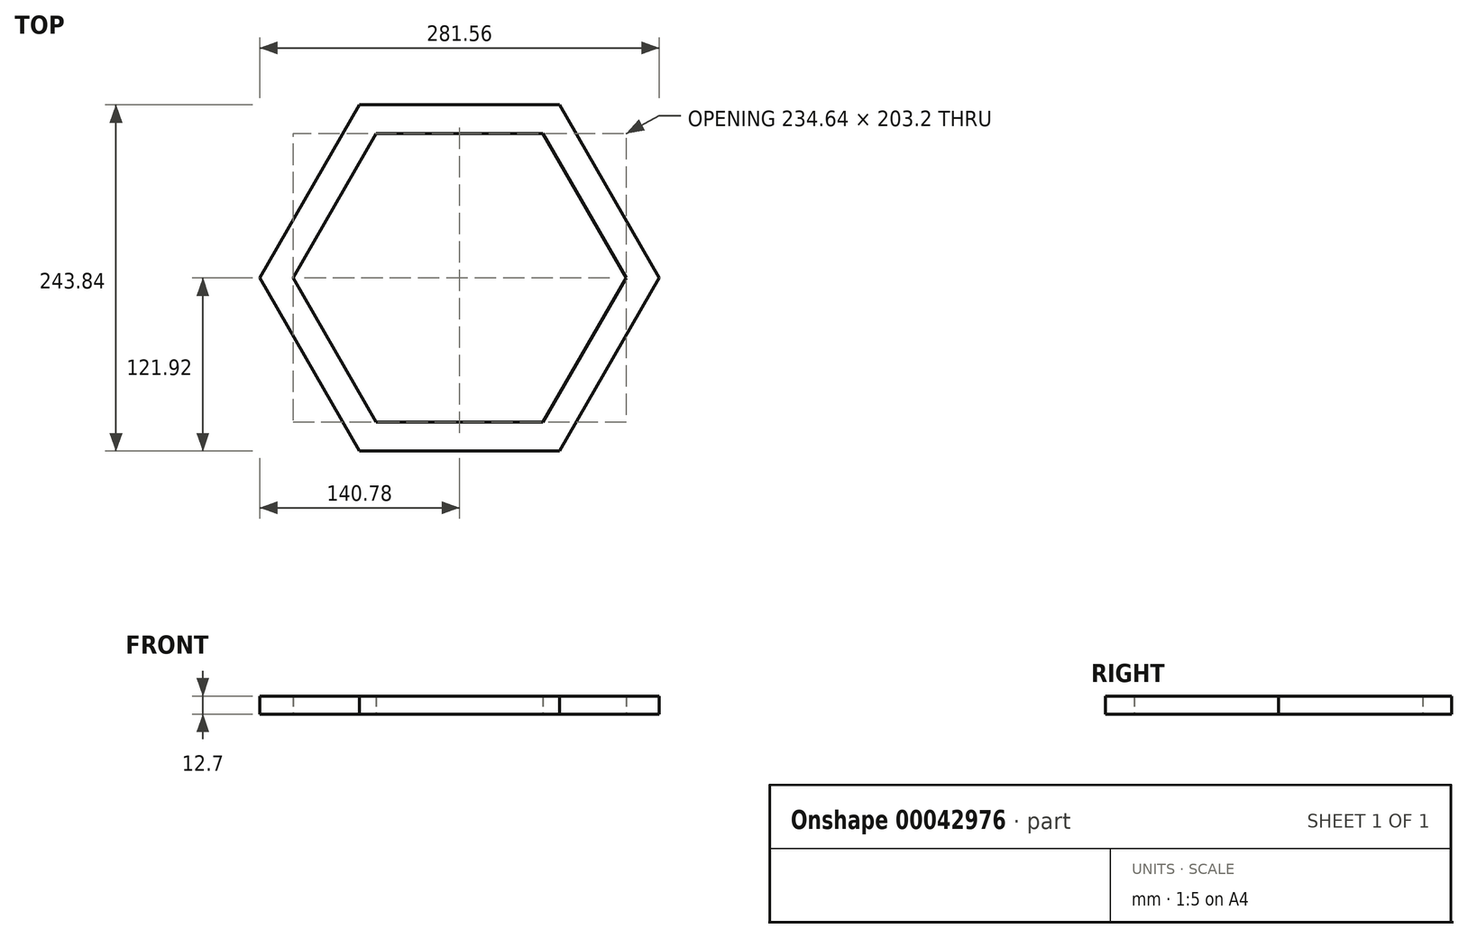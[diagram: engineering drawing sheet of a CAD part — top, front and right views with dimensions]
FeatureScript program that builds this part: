
annotation { "Feature Type Name" : "Feature", "Feature Type Description" : "" }
export const myFeature = defineFeature(function(context is Context, id is Id, definition is map)
    precondition{}
    {
        {
            var Q0;
            Q0=qCreatedBy(makeId("Top.planeOp"),FACE);
            var sketch = newSketch(context, id + "F0", { "sketchPlane" : qUnion([Q0])});
            skCircle(sketch, "E0.cCircle", {"center": v(0, 0) * mm, "radius": 101.6 * mm, "construction": true});
            skLineSegment(sketch, "E0.0", {"start": v(58.66, 101.6) * mm, "end": v(117.32, 0) * mm});
            skLineSegment(sketch, "E0.1", {"start": v(117.32, 0) * mm, "end": v(58.66, -101.6) * mm});
            skLineSegment(sketch, "E0.2", {"start": v(58.66, -101.6) * mm, "end": v(-58.66, -101.6) * mm});
            skLineSegment(sketch, "E0.3", {"start": v(-58.66, -101.6) * mm, "end": v(-117.32, 0) * mm});
            skLineSegment(sketch, "E0.4", {"start": v(-117.32, 0) * mm, "end": v(-58.66, 101.6) * mm});
            skLineSegment(sketch, "E0.5", {"start": v(-58.66, 101.6) * mm, "end": v(58.66, 101.6) * mm});
            skPoint(sketch, "E0.0.midPoint", {"position": v(87.99, 50.8) * mm});
            skLineSegment(sketch, "E1", {"start": v(-117.32, 0) * mm, "end": v(117.32, 0) * mm, "construction": true});
            skCircle(sketch, "E2.cCircle", {"center": v(0, 0) * mm, "radius": 121.92 * mm, "construction": true});
            skLineSegment(sketch, "E2.0", {"start": v(70.4, 121.92) * mm, "end": v(140.78, 0) * mm});
            skLineSegment(sketch, "E2.1", {"start": v(140.78, 0) * mm, "end": v(70.4, -121.92) * mm});
            skLineSegment(sketch, "E2.2", {"start": v(70.4, -121.92) * mm, "end": v(-70.4, -121.92) * mm});
            skLineSegment(sketch, "E2.3", {"start": v(-70.4, -121.92) * mm, "end": v(-140.78, 0) * mm});
            skLineSegment(sketch, "E2.4", {"start": v(-140.78, 0) * mm, "end": v(-70.4, 121.92) * mm});
            skLineSegment(sketch, "E2.5", {"start": v(-70.4, 121.92) * mm, "end": v(70.4, 121.92) * mm});
            skPoint(sketch, "E2.0.midPoint", {"position": v(105.59, 60.96) * mm});
            skSolve(sketch);
        }
        {
            var Q0;
            Q0=makeQuery(id+"F0.imprint","IMPRINT",FACE,{"disambiguationData":[TD([[makeQuery(id+"F0.imprint","IMPRINT",EDGE,{"derivedFrom":sQuery(id+"F0.wireOp",EDGE,"E0.0")}),1.0]])]});
            extrude(context, id + "F1", {"entities" : qUnion([Q0]), "endBound" : BoundingType.SYMMETRIC, "depth" : 12.7 * mm});
        }
    });
